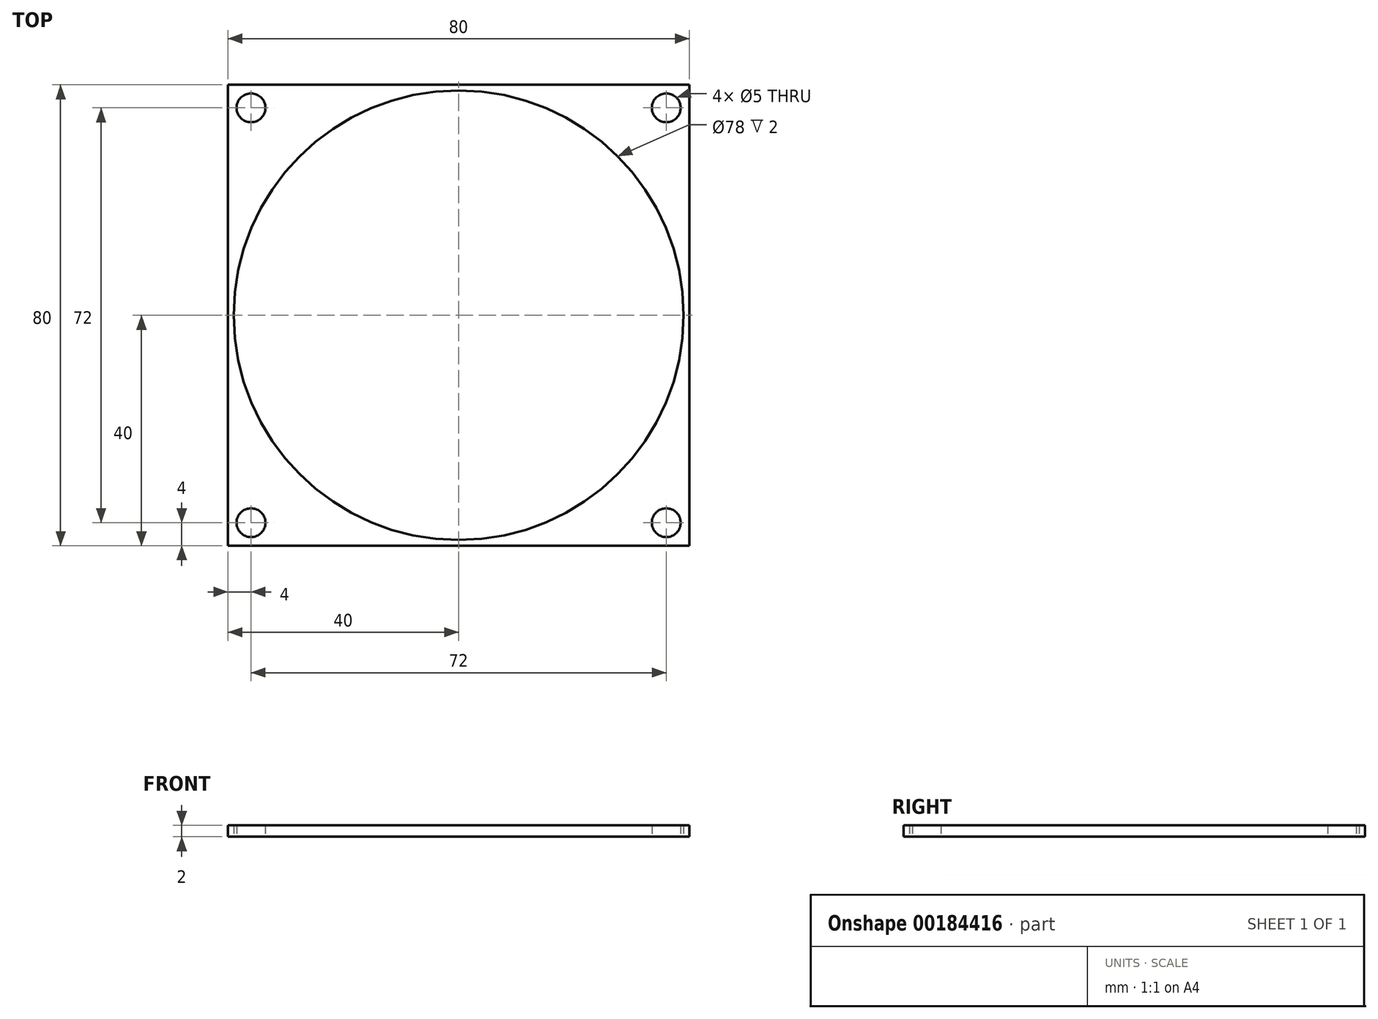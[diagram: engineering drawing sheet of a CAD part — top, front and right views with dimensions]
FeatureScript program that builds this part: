
annotation { "Feature Type Name" : "Feature", "Feature Type Description" : "" }
export const myFeature = defineFeature(function(context is Context, id is Id, definition is map)
    precondition{}
    {
        {
            var Q0;
            Q0=qCreatedBy(makeId("Top.planeOp"),FACE);
            var sketch = newSketch(context, id + "F0", { "sketchPlane" : qUnion([Q0])});
            skLineSegment(sketch, "E0.bottom", {"start": v(40, -40) * mm, "end": v(-40, -40) * mm});
            skLineSegment(sketch, "E0.top", {"start": v(40, 40) * mm, "end": v(-40, 40) * mm});
            skLineSegment(sketch, "E0.left", {"start": v(40, -40) * mm, "end": v(40, 40) * mm});
            skLineSegment(sketch, "E0.right", {"start": v(-40, -40) * mm, "end": v(-40, 40) * mm});
            skPoint(sketch, "E0.middle", {"position": v(0, 0) * mm});
            skCircle(sketch, "E1", {"center": v(-36, -36) * mm, "radius": 2.5 * mm});
            skCircle(sketch, "E2", {"center": v(0, 0) * mm, "radius": 39 * mm});
            skLineSegment(sketch, "E3", {"start": v(0, -40) * mm, "end": v(0, 40) * mm, "construction": true});
            skLineSegment(sketch, "E4", {"start": v(-40, 0) * mm, "end": v(40, 0) * mm, "construction": true});
            skCircle(sketch, "E5.MirrorC", {"center": v(36, -36) * mm, "radius": 2.5 * mm});
            skCircle(sketch, "E6.MirrorC", {"center": v(-36, 36) * mm, "radius": 2.5 * mm});
            skCircle(sketch, "E7.MirrorC", {"center": v(36, 36) * mm, "radius": 2.5 * mm});
            skSolve(sketch);
        }
        {
            var Q0;
            Q0=makeQuery(id+"F0.imprint","IMPRINT",FACE,{"disambiguationData":[TD([[makeQuery(id+"F0.imprint","IMPRINT",EDGE,{"derivedFrom":sQuery(id+"F0.wireOp",EDGE,"E0.bottom")}),-1.0]])]});
            extrude(context, id + "F1", {"entities" : qUnion([Q0]), "depth" : 2 * mm});
        }
    });
